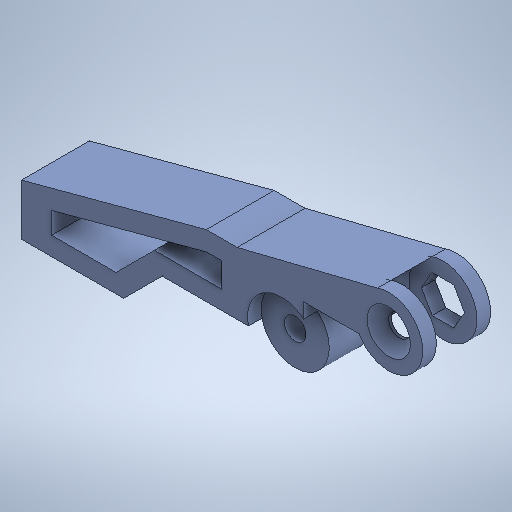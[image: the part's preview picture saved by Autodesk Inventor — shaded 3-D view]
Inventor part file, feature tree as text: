
AUTODESK INVENTOR PART (.ipt)
format: ipt  version: 2025.2 (Build 292293000, 293)  size: 367,104 bytes
history: native  units: mm
features: sketch x5, extrude x5, hole x2, other x1, pattern_linear x1
ambient origin geometry x8: Origin, YZ Plane, XZ Plane, XY Plane, X Axis, Y Axis, Z Axis, Center Point
bodies: Body1 (feature_tree)
feature tree (14):
  other  "Sólido1"
  sketch  "Esboço1"  dims[d2=2.2mm d3=0.0mm d4=11.0mm]
  extrude  "Extrusão1"  Depth=11.0mm
  extrude  "Extrusão2"  Depth=9.3mm
  extrude  "Extrusão3"  Depth=22.3mm
  hole  "Furo1"  [1 undecoded]
  hole  "Furo2"  [1 undecoded]
  pattern_linear  "Padrão retangular3"  Spacing1=135.0deg  [1 undecoded]
  extrude  "Extrusão6"  Depth=6.6mm
  extrude  "Extrusão7"  Depth=6.6mm
  sketch  "Esboço2"  dims[d5=28.2mm d6=9.3mm]
  sketch  "Esboço3"  dims[d7=65.0mm d8=22.3mm]
  sketch  "Esboço4"  dims[d9=65.0mm d10=9.35mm]
  sketch  "Esboço6"  dims[d11=17.35mm d12=8.8mm d14=135.0deg d15=14.0mm d16=8.3mm d17=31.0mm d18=105.0deg d19=5.0mm d20=2.443461mm d21=2.45mm d22=9.0mm d23=3.0mm d24=3.0mm d25=3.5mm d26=3.0mm d27=3.0mm d28=4.0mm d29=2.5mm d30=6.6mm d31=0.0mm d32=2.2mm d33=0.0mm d34=3.5mm d35=6.0mm d36=4.0mm d37=2.0mm d38=90.0deg d39=8.0mm d40=20.594885mm d41=3.5mm d42=6.0mm d43=7.0mm d44=2.0mm d45=90.0deg d46=8.0mm d47=20.594885mm d63=20.0mm d65=8.8mm d66=4.4mm d67=0.0mm d68=6.6mm d69=0.0mm d56=0.5mm d57=0.872665mm d58=0.5mm d59=0.872665mm d60=0.872665mm d61=0.5mm d62=0.872665mm d64=0.872665mm d70=0.5mm d71=0.872665mm d72=0.5mm d73=0.872665mm]
note: 3 required parameter values undecoded (feature->parameter linkage not recoverable at this tier; creation-order binding heuristic only, values carry confidence <= 0.55)
